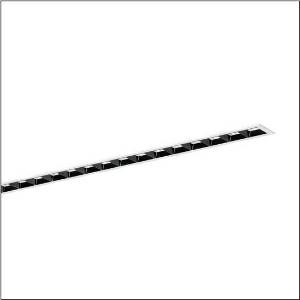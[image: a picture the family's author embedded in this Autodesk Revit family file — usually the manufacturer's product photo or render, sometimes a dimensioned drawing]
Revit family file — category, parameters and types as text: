
# Revit family: silica_r__21_51mx12tat4w_4f36
name_source: partatom
category: Lighting Fixtures
units: mm (PartAtom-declared; Revit-internal decimal feet)

## family parameters
Cut with Voids When Loaded = No
Host = Face
Light Source = No
Part Type = Normal
Room Calculation Point = No
Round Connector Dimension = Use Diameter
Shared = No

## types (1)
- --- (1 x LED, 3720 lm, 32.1 W, 6500K)
    Apparent Load = 32 VA
    CIE Flux Codes = 84 100 100 100 100
    Color Rendering = 80
    Color Temperature = 6500K
    Default Elevation = 1800 mm
    Description = Silica® 21, office luminaire, primary light control with darklight reflector, of PMMA, black, CAT 2 (L<= 3000cd/m²), light emission: direct distribution, primary light characteristic: symmetric, installation type: recessed, LED, rated luminous flux: 3.720lm, luminous efficacy: 110lm/W, light colour: 8tw, colour temperature: 2700..6500K, with terminal, 3+2-pole, max. 2.5mm², mains connection: 220..240V, AC, 50/60Hz, rated input power: 33.8W, luminaire housing, of aluminium, traffic white (RAL 9016), length: 1.228mm, width: 79mm, height: 53mm, protection rating (complete): IP20, insulation class (complete): insulation class I (protective earthing), certification: CE, permissible operating ambient temperature: 0..+35°C, standard: EN 50419, packaging unit: 1 piece
    Height = 0 mm  [stored 0 ft]
    Lamp = 1 x LED
    Lamp Light Flux = 3720 lm
    Lamp Power = 32.1 W
    Lamp count = 1
    Length = 1227 mm
    Luminous efficacy = 116 lm/W
    Manufacturer = Siteco
    ModVariant = No
    Model = 51MX12TAT4W
    Mounting Place = Ceiling
    Mounting Type = Recessed
    Number of Poles = 1
    OnlyDefault = Yes
    Power Factor = 1
    Product Name = Silica® 21
    Product group = office luminaire | ceiling recessed
    ProductGroupID = 400
    Protection Class = Protection class I
    Protection Degree = IP 20
    RLX_Detail_Level = 1
    RlxData = <blob elided: 35545 chars, md5=bc6b32fa>
    Socket = socket
    Standby Power = 0 W
    System Light Flux = 3720 lm
    System Power = 32 W
    Type Comments = individual setting
    Type Image = l_1251632.jpg
    URL = http://relux.com
    VarID = @adj_046269
    Voltage = 0 V
    Weight = 0.00 kg
    Width = 79 mm

note: [stored X ft] marks values corroborated as IEEE doubles in the binary element streams (Revit-internal decimal feet)

## geometry (parser evidence)
native form markers: Blend x4, Sweep x8
no freeform markers — native parametric forms only
